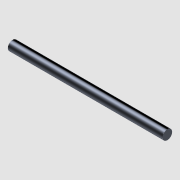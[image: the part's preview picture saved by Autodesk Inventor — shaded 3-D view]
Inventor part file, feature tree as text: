
AUTODESK INVENTOR PART (.ipt)
format: ipt  version: 2021 (Build 250183000, 183)  size: 101,888 bytes
history: native  units: in
note: dims shown in document units (in); Inventor stores cm internally (conversion verified against a paired STEP export)
features: extrude x2, other x1, imported_body x1, sketch x1
ambient origin geometry x8: Origin, YZ Plane, XZ Plane, XY Plane, X Axis, Y Axis, Z Axis, Center Point
bodies: Body1 (feature_tree)
feature tree (5):
  other  "Pin"
  extrude  "Extrude1"  TaperAngle=0.0deg  [1 undecoded]
  extrude  "Extrusion1"  [1 undecoded]
  imported_body  "Base1"
  sketch  "Sketch1"  dims[d1=0.5in d2=0.0in]
note: 2 required parameter values undecoded (feature->parameter linkage not recoverable at this tier; creation-order binding heuristic only, values carry confidence <= 0.55)
